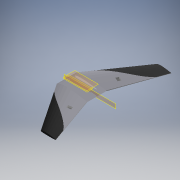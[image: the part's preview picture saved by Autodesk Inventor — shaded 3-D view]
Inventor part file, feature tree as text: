
AUTODESK INVENTOR PART (.ipt)
format: ipt  version: 2017 (Build 210142000, 142)  size: 2,505,216 bytes
history: native  units: mm
features: plane x4, other x3, extrude x3, sketch x3, split x1, mirror x1, projected_geometry x1
ambient origin geometry x8: Origin, YZ Plane, XZ Plane, XY Plane, X Axis, Y Axis, Z Axis, Center Point
bodies: Solid1 (feature_tree)
feature tree (16):
  other  "Asa 1.ipt"
  plane  "Work Plane2"
  extrude  "Extrusion2"  Depth=393.7mm
  extrude  "Extrusion3"  Depth=69.75mm TaperAngle=0.0deg
  plane  "Work Plane3"
  plane  "Work Plane5"
  extrude  "Extrusion5"  Depth=46.0mm
  split  "Split1"
  mirror  "Mirror1"
  plane  "Work Plane4"
  other  "Solid1::Asa 1.ipt"
  other  "TaggingFeature1"
  sketch  "Sketch3"  dims[d0=393.7mm d2=61.25mm]
  sketch  "Sketch4"  dims[d12=51.0mm d13=0.0mm d14=69.75mm d15=0.0mm]
  sketch  "Sketch7"  dims[d16=79.0mm d21=60.5mm d24=69.5mm d25=0.0mm d29=58.0mm d30=46.0mm]
  projected_geometry  "Projected Loop1"
